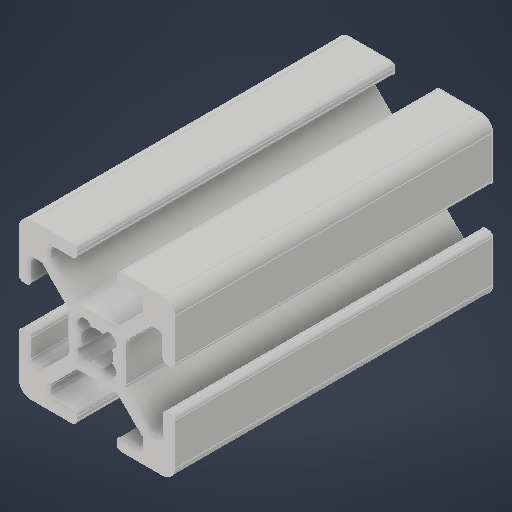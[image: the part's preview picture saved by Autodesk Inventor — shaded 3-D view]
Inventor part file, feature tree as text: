
AUTODESK INVENTOR PART (.ipt)
format: ipt  version: 2025 (Build 290162000, 162)  size: 404,480 bytes
history: native  units: mm
features: extrude x2, sketch x2
ambient origin geometry x8: Origin, YZ Plane, XZ Plane, XY Plane, X Axis, Y Axis, Z Axis, Center Point
bodies: Solid1 (feature_tree)
feature tree (4):
  extrude  "Extrusion1"  Depth=13.0mm
  extrude  "Extrusion2"  Depth=4.0mm
  sketch  "Sketch_1"  dims[d0=41.0mm d1=0.0mm d2=13.0mm]
  sketch  "Sketch2"  dims[d3=4.0mm d4=4.0mm d5=0.0mm d6=0.0mm]
